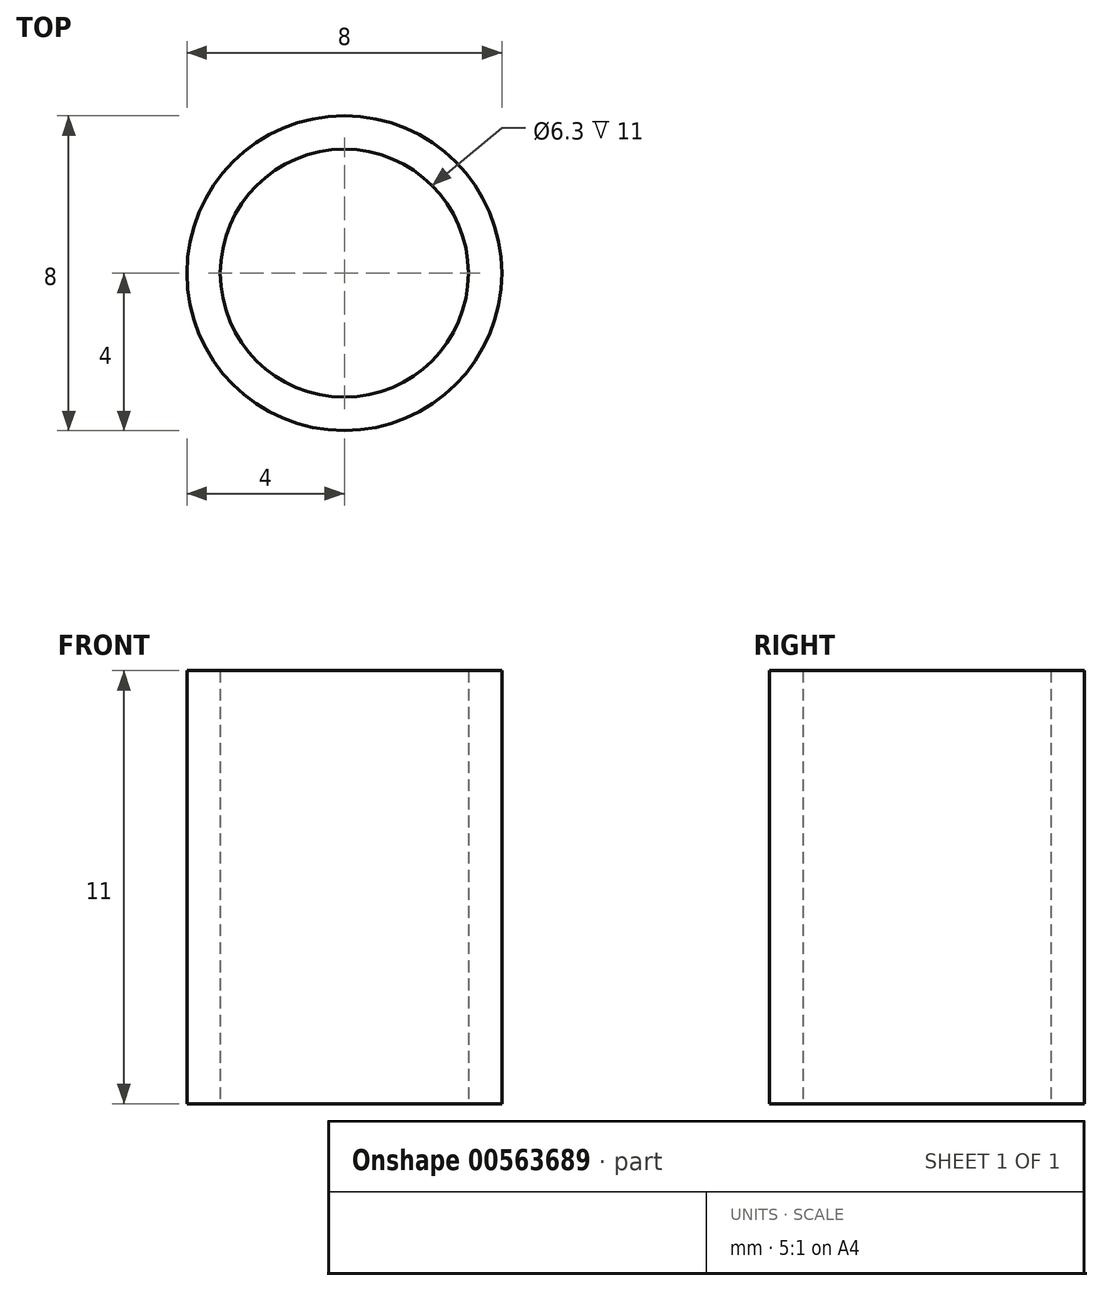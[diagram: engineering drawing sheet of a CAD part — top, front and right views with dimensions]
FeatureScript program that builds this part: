
annotation { "Feature Type Name" : "Feature", "Feature Type Description" : "" }
export const myFeature = defineFeature(function(context is Context, id is Id, definition is map)
    precondition{}
    {
        {
            var Q0;
            Q0=qCreatedBy(makeId("Top.planeOp"),FACE);
            var sketch = newSketch(context, id + "F0", { "sketchPlane" : qUnion([Q0])});
            skCircle(sketch, "E0", {"center": v(0, 0) * mm, "radius": 3.15 * mm});
            skCircle(sketch, "E1", {"center": v(0, 0) * mm, "radius": 4 * mm});
            skSolve(sketch);
        }
        {
            var Q0;
            Q0=makeQuery(id+"F0.imprint","IMPRINT",FACE,{"disambiguationData":[TD([[makeQuery(id+"F0.imprint","IMPRINT",EDGE,{"derivedFrom":sQuery(id+"F0.wireOp",EDGE,"E0")}),-1.0]])]});
            extrude(context, id + "F1", {"entities" : qUnion([Q0]), "depth" : 11 * mm, "offsetDistance" : 25 * mm});
        }
    });
